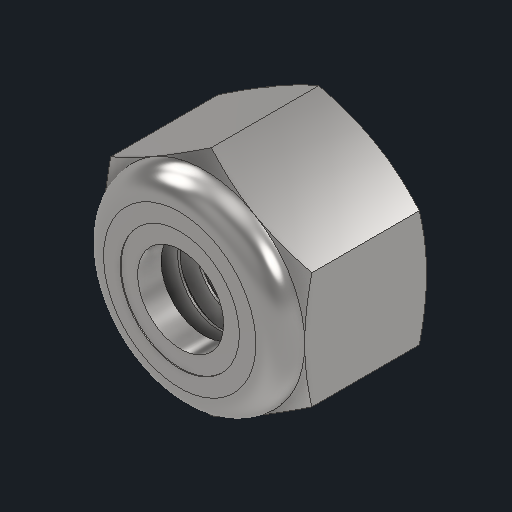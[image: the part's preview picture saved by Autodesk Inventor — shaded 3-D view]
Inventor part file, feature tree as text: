
AUTODESK INVENTOR PART (.ipt)
format: ipt  version: 2024.1 (Build 281209000, 209)  size: 389,120 bytes
history: native  units: in
note: dims shown in document units (in); Inventor stores cm internally (conversion verified against a paired STEP export)
features: revolve x1, other x1
ambient origin geometry x8: Origin, YZ Plane, XZ Plane, XY Plane, X Axis, Y Axis, Z Axis, Center Point
bodies: Solid1 (feature_tree), Solid2 (feature_tree)
feature tree (2):
  revolve  "Revolve1"  [1 undecoded]
  other  "Cut-Extrude2"
note: 1 required parameter value undecoded (feature->parameter linkage not recoverable at this tier; creation-order binding heuristic only, values carry confidence <= 0.55)
